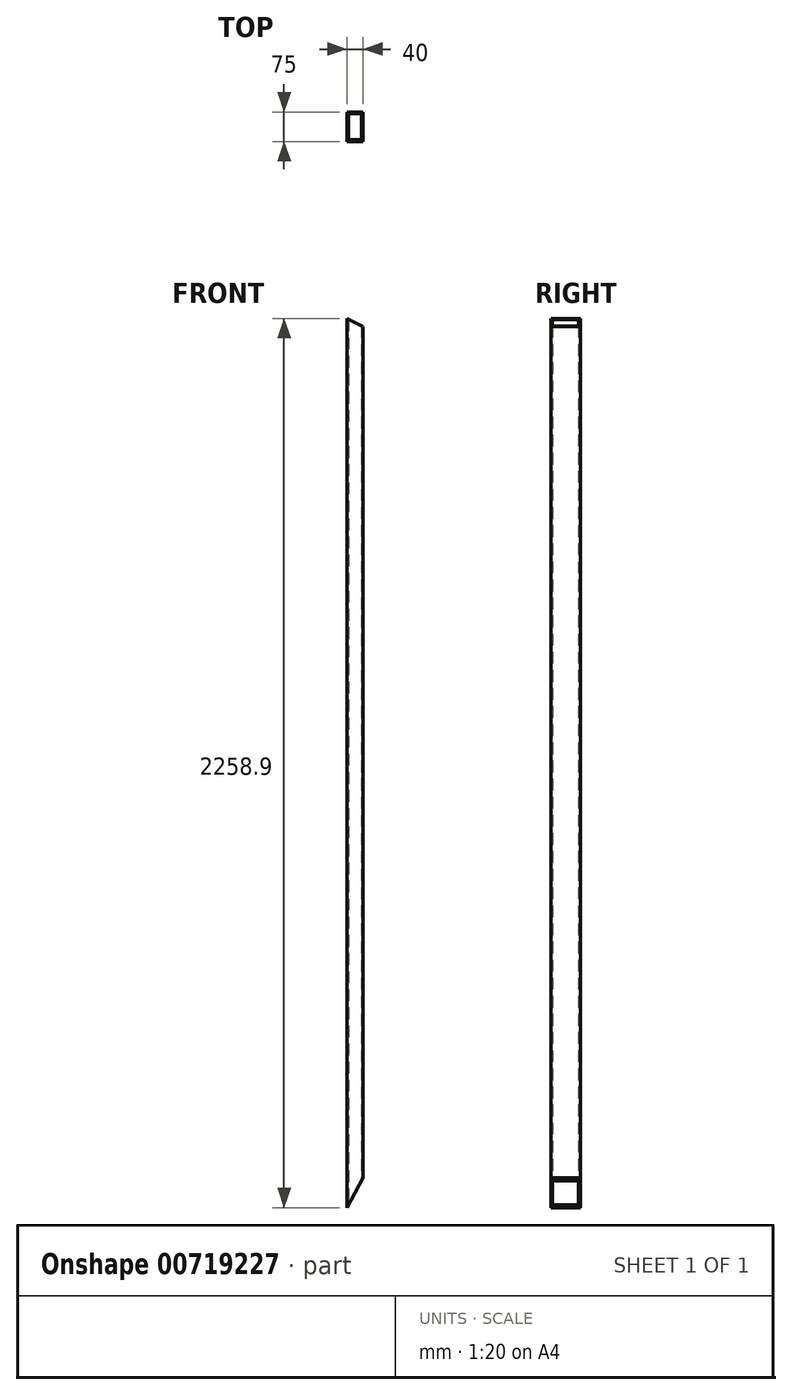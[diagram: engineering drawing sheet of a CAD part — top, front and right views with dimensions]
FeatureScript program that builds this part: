
annotation { "Feature Type Name" : "Feature", "Feature Type Description" : "" }
export const myFeature = defineFeature(function(context is Context, id is Id, definition is map)
    precondition{}
    {
        {
            var Q0;
            Q0=qCreatedBy(makeId("Top.planeOp"),FACE);
            var sketch = newSketch(context, id + "F0", { "sketchPlane" : qUnion([Q0])});
            skLineSegment(sketch, "E0.bottom", {"start": v(0, 0) * mm, "end": v(40, 0) * mm});
            skLineSegment(sketch, "E0.top", {"start": v(0, 75) * mm, "end": v(40, 75) * mm});
            skLineSegment(sketch, "E0.left", {"start": v(0, 0) * mm, "end": v(0, 75) * mm});
            skLineSegment(sketch, "E0.right", {"start": v(40, 0) * mm, "end": v(40, 75) * mm});
            skLineSegment(sketch, "E1.0", {"start": v(4, 71) * mm, "end": v(36, 71) * mm});
            skLineSegment(sketch, "E1.1", {"start": v(4, 4) * mm, "end": v(4, 71) * mm});
            skLineSegment(sketch, "E1.2", {"start": v(4, 4) * mm, "end": v(36, 4) * mm});
            skLineSegment(sketch, "E1.3", {"start": v(36, 4) * mm, "end": v(36, 71) * mm});
            skSolve(sketch);
        }
        {
            var Q0;
            Q0=makeQuery(id+"F0.imprint","IMPRINT",FACE,{"disambiguationData":[TD([[makeQuery(id+"F0.imprint","IMPRINT",EDGE,{"derivedFrom":sQuery(id+"F0.wireOp",EDGE,"E0.bottom")}),1.0]])]});
            extrude(context, id + "F1", {"entities" : qUnion([Q0]), "depth" : 2258.9 * mm, "offsetDistance" : 25 * mm});
        }
        {
            var Q0;
            Q0=makeQuery(id+"F1.opExtrude","SWEPT_FACE",FACE,{"disambiguationData":[OSD([sQuery(id+"F0.wireOp",EDGE,"E0.top")])]});
            var sketch = newSketch(context, id + "F2", { "sketchPlane" : qUnion([Q0])});
            skLineSegment(sketch, "E2", {"start": v(0, 2258.9) * mm, "end": v(-40, 2237.9) * mm});
            skSolve(sketch);
        }
        {
            var Q0;
            {var subQ0=sQuery(id+"F2.wireOp",EDGE,"E2");Q0=makeQuery(id+"F2.imprint","IMPRINT",FACE,{"disambiguationData":[TD([[makeQuery(id+"F2.imprint","IMPRINT",EDGE,{"derivedFrom":subQ0}),-1.0]])]});}
            var Q1;
            Q1=makeQuery(id+"F1.opExtrude","SWEPT_FACE",FACE,{"disambiguationData":[OSD([sQuery(id+"F0.wireOp",EDGE,"E0.bottom")])]});
            extrude(context, id + "F3", {"entities" : qUnion([Q0]), "operationType" : NewBodyOperationType.REMOVE, "endBound" : BoundingType.UP_TO_SURFACE, "oppositeDirection" : true, "depth" : 25 * mm, "endBoundEntityFace" : qUnion([Q1]), "offsetDistance" : 25 * mm});
        }
        {
            var Q0;
            Q0=makeQuery(id+"F1.opExtrude","SWEPT_FACE",FACE,{"disambiguationData":[OSD([sQuery(id+"F0.wireOp",EDGE,"E0.top")])]});
            var sketch = newSketch(context, id + "F4", { "sketchPlane" : qUnion([Q0])});
            skLineSegment(sketch, "E3", {"start": v(0, 0) * mm, "end": v(-40, 76.19) * mm});
            skSolve(sketch);
        }
        {
            var Q0;
            {var subQ0=sQuery(id+"F4.wireOp",EDGE,"E3");Q0=makeQuery(id+"F4.imprint","IMPRINT",FACE,{"disambiguationData":[TD([[makeQuery(id+"F4.imprint","IMPRINT",EDGE,{"derivedFrom":subQ0}),1.0]])]});}
            var Q1;
            Q1=makeQuery(id+"F1.opExtrude","SWEPT_FACE",FACE,{"disambiguationData":[OSD([sQuery(id+"F0.wireOp",EDGE,"E0.bottom")])]});
            extrude(context, id + "F5", {"entities" : qUnion([Q0]), "operationType" : NewBodyOperationType.REMOVE, "endBound" : BoundingType.UP_TO_SURFACE, "oppositeDirection" : true, "depth" : 25 * mm, "endBoundEntityFace" : qUnion([Q1]), "offsetDistance" : 25 * mm});
        }
    });
